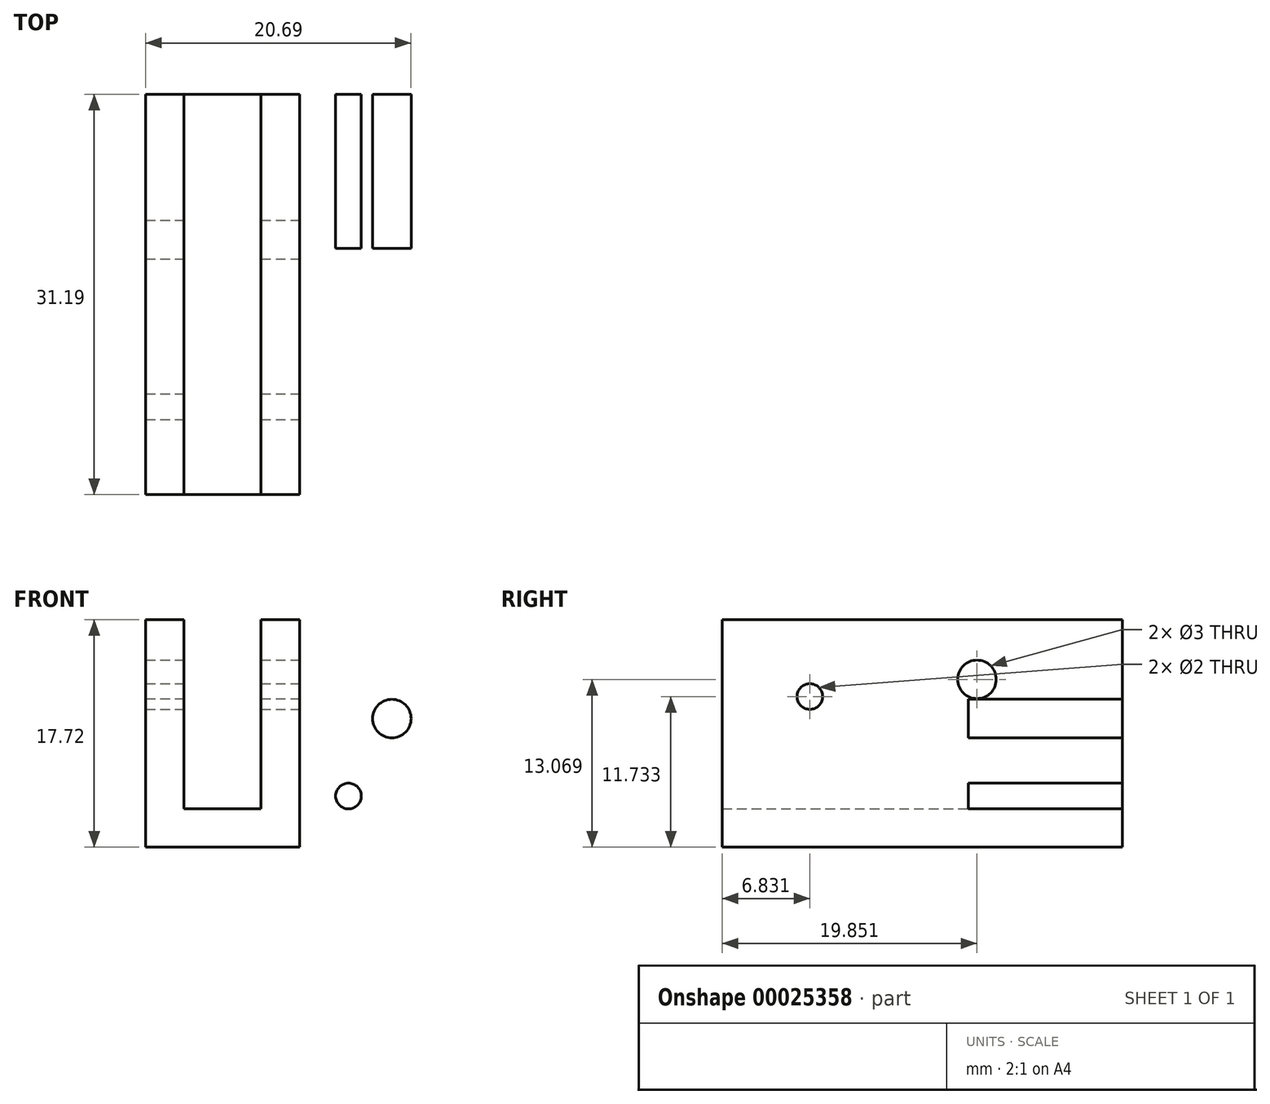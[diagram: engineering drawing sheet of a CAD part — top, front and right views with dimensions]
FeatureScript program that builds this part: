
annotation { "Feature Type Name" : "Feature", "Feature Type Description" : "" }
export const myFeature = defineFeature(function(context is Context, id is Id, definition is map)
    precondition{}
    {
        {
            var Q0;
            Q0=qCreatedBy(makeId("Front.planeOp"),FACE);
            var sketch = newSketch(context, id + "F0", { "sketchPlane" : qUnion([Q0])});
            skLineSegment(sketch, "E0.bottom", {"start": v(-5.76, 17.72) * mm, "end": v(6.24, 17.72) * mm});
            skLineSegment(sketch, "E0.top", {"start": v(-5.76, 0) * mm, "end": v(6.24, 0) * mm});
            skLineSegment(sketch, "E0.left", {"start": v(-5.76, 17.72) * mm, "end": v(-5.76, 0) * mm});
            skLineSegment(sketch, "E0.right", {"start": v(6.24, 17.72) * mm, "end": v(6.24, 0) * mm});
            skLineSegment(sketch, "E1.bottom", {"start": v(-2.76, 17.72) * mm, "end": v(3.24, 17.72) * mm});
            skLineSegment(sketch, "E1.top", {"start": v(-2.76, 3) * mm, "end": v(3.24, 3) * mm});
            skLineSegment(sketch, "E1.left", {"start": v(-2.76, 17.72) * mm, "end": v(-2.76, 3) * mm});
            skLineSegment(sketch, "E1.right", {"start": v(3.24, 17.72) * mm, "end": v(3.24, 3) * mm});
            skSolve(sketch);
        }
        {
            var Q0;
            Q0=makeQuery(id+"F0.imprint","IMPRINT",FACE,{"disambiguationData":[TD([[makeQuery(id+"F0.imprint","IMPRINT",EDGE,{"derivedFrom":sQuery(id+"F0.wireOp",EDGE,"E0.top")}),1.0]])]});
            extrude(context, id + "F1", {"entities" : qUnion([Q0]), "depth" : 31.2 * mm});
        }
        {
            var Q0;
            Q0=makeQuery(id+"F1.opExtrude","SWEPT_FACE",FACE,{"disambiguationData":[OSD([sQuery(id+"F0.wireOp",EDGE,"E0.right")])]});
            var sketch = newSketch(context, id + "F2", { "sketchPlane" : qUnion([Q0])});
            skCircle(sketch, "E2", {"center": v(-24.36, 11.73) * mm, "radius": 1 * mm});
            skCircle(sketch, "E3", {"center": v(-11.34, 13.07) * mm, "radius": 1.5 * mm});
            skSolve(sketch);
        }
        {
            var Q0;
            Q0 = qSketchRegion(id + "F2", true);
            extrude(context, id + "F3", {"entities" : qUnion([Q0]), "operationType" : NewBodyOperationType.REMOVE, "oppositeDirection" : true, "depth" : 25 * mm});
        }
        {
            var Q0;
            Q0=qCreatedBy(makeId("Front.planeOp"),FACE);
            var sketch = newSketch(context, id + "F4", { "sketchPlane" : qUnion([Q0])});
            skCircle(sketch, "E4", {"center": v(13.43, 10.02) * mm, "radius": 1.5 * mm});
            skCircle(sketch, "E5", {"center": v(10.05, 3.98) * mm, "radius": 1 * mm});
            skSolve(sketch);
        }
        {
            var Q0;
            Q0 = qSketchRegion(id + "F4", true);
            extrude(context, id + "F5", {"entities" : qUnion([Q0]), "depth" : 12 * mm});
        }
    });
